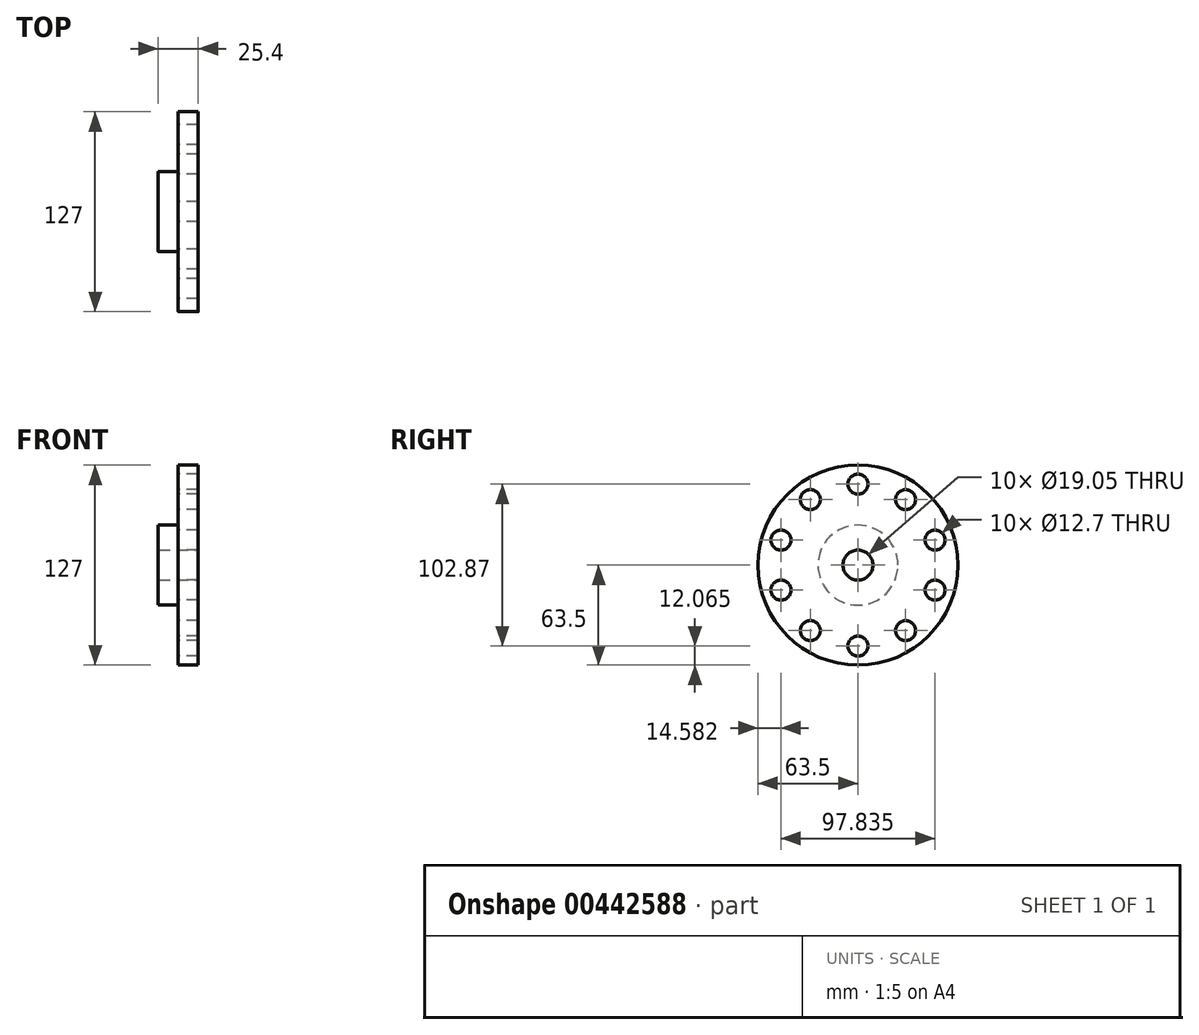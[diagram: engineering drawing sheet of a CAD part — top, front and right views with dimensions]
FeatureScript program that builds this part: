
annotation { "Feature Type Name" : "Feature", "Feature Type Description" : "" }
export const myFeature = defineFeature(function(context is Context, id is Id, definition is map)
    precondition{}
    {
        {
            var Q0;
            Q0=qCreatedBy(makeId("Front.planeOp"),FACE);
            var sketch = newSketch(context, id + "F0", { "sketchPlane" : qUnion([Q0])});
            skLineSegment(sketch, "E0", {"start": v(0, 0) * mm, "end": v(0, 38.1) * mm});
            skLineSegment(sketch, "E1", {"start": v(0, 38.1) * mm, "end": v(12.7, 38.1) * mm});
            skLineSegment(sketch, "E2", {"start": v(12.7, 38.1) * mm, "end": v(12.7, -15.87) * mm});
            skLineSegment(sketch, "E3", {"start": v(12.7, -15.87) * mm, "end": v(-12.7, -15.87) * mm});
            skLineSegment(sketch, "E4", {"start": v(-12.7, -15.88) * mm, "end": v(-12.7, 0) * mm});
            skLineSegment(sketch, "E5", {"start": v(-12.7, 0) * mm, "end": v(0, 0) * mm});
            skLineSegment(sketch, "E6", {"start": v(12.7, -15.87) * mm, "end": v(12.7, -25.4) * mm});
            skLineSegment(sketch, "E7", {"start": v(12.7, -25.4) * mm, "end": v(-30.04, -25.4) * mm});
            skSolve(sketch);
        }
        {
            var Q0;
            Q0=makeQuery(id+"F0.imprint","IMPRINT",FACE,{"disambiguationData":[TD([[makeQuery(id+"F0.imprint","IMPRINT",EDGE,{"derivedFrom":sQuery(id+"F0.wireOp",EDGE,"E0")}),-1.0]])]});
            var Q1;
            Q1=sQuery(id+"F0.wireOp",EDGE,"E7");
            revolve(context, id + "F1", {"entities" : qUnion([Q0]), "axis" : qUnion([Q1]), "revolveType" : RevolveType.FULL});
        }
        {
            var Q0;
            Q0=makeQuery(id+"F1.opRevolve","SWEPT_FACE",FACE,{"disambiguationData":[OSD([sQuery(id+"F0.wireOp",EDGE,"E4")])]});
            var sketch = newSketch(context, id + "F2", { "sketchPlane" : qUnion([Q0])});
            skLineSegment(sketch, "E8", {"start": v(0, -15.87) * mm, "end": v(0, 26.04) * mm});
            skPoint(sketch, "E9", {"position": v(0, 26.04) * mm});
            skSolve(sketch);
        }
        {
            var Q0;
            Q0=sQuery(id+"F2.wireOp",VERTEX,"E9");
            var Q1;
            Q1=makeQuery(id+"F1.opRevolve","SWEPT_BODY",BODY,{"disambiguationData":[OSD([sQuery(id+"F0.wireOp",EDGE,"E0"),sQuery(id+"F0.wireOp",EDGE,"E1"),sQuery(id+"F0.wireOp",EDGE,"E2"),sQuery(id+"F0.wireOp",EDGE,"E3"),sQuery(id+"F0.wireOp",EDGE,"E4"),sQuery(id+"F0.wireOp",EDGE,"E5")])]});
            hole(context, id + "F3", {"style" : HoleStyle.SIMPLE, "endStyle" : HoleEndStyle.THROUGH, "holeDiameter" : 12.7 * mm, "isTappedThrough" : true, "tappedDepth" : 12.7 * mm, "tapClearance" : 3, "locations" : qUnion([Q0]), "scope" : qUnion([Q1])});
        }
        {
            var Q0;
            Q0=makeQuery(id+"F1.opRevolve","SWEPT_BODY",BODY,{"disambiguationData":[OSD([sQuery(id+"F0.wireOp",EDGE,"E0"),sQuery(id+"F0.wireOp",EDGE,"E1"),sQuery(id+"F0.wireOp",EDGE,"E2"),sQuery(id+"F0.wireOp",EDGE,"E3"),sQuery(id+"F0.wireOp",EDGE,"E4"),sQuery(id+"F0.wireOp",EDGE,"E5")])]});
            var Q1;
            Q1=makeQuery(id+"F1.opRevolve","SWEPT_EDGE",EDGE,{"disambiguationData":[OSD([sQuery(id+"F0.wireOp",EDGE,"E3"),sQuery(id+"F0.wireOp",EDGE,"E4")])]});
            circularPattern(context, id + "F4", {"entities" : qUnion([Q0]), "axis" : qUnion([Q1]), "angle" : 360 * degree, "instanceCount" : 10, "equalSpace" : true});
        }
    });
